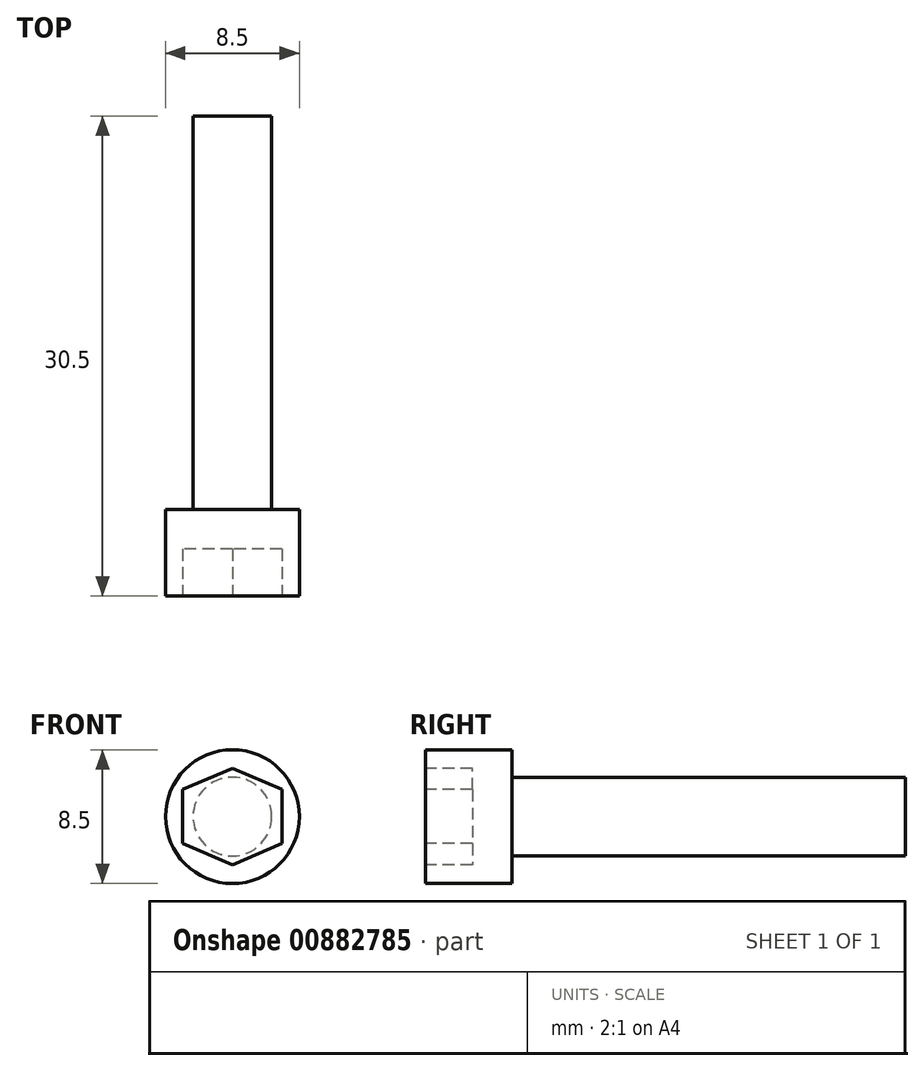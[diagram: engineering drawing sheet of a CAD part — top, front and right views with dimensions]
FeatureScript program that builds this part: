
annotation { "Feature Type Name" : "Feature", "Feature Type Description" : "" }
export const myFeature = defineFeature(function(context is Context, id is Id, definition is map)
    precondition{}
    {
        {
            var Q0;
            Q0=qCreatedBy(makeId("Front.planeOp"),FACE);
            var sketch = newSketch(context, id + "F0", { "sketchPlane" : qUnion([Q0])});
            skCircle(sketch, "E0", {"center": v(0, 0) * mm, "radius": 4.25 * mm});
            skSolve(sketch);
        }
        {
            var Q0;
            Q0 = qSketchRegion(id + "F0", true);
            extrude(context, id + "F1", {"entities" : qUnion([Q0]), "depth" : 5.5 * mm, "offsetDistance" : 25.4 * mm});
        }
        {
            var Q0;
            Q0=makeQuery(id+"F1.opExtrude","CAP_FACE",FACE,{"disambiguationData":[OSD([sQuery(id+"F0.wireOp",EDGE,"E0")])],"isStart":false});
            var sketch = newSketch(context, id + "F2", { "sketchPlane" : qUnion([Q0])});
            skLineSegment(sketch, "E1", {"start": v(0, 4.25) * mm, "end": v(0, -4.25) * mm});
            skLineSegment(sketch, "E2", {"start": v(4.25, 0) * mm, "end": v(-4.25, 0) * mm});
            skLineSegment(sketch, "E3", {"start": v(0, 3.07) * mm, "end": v(-3.15, 1.71) * mm});
            skLineSegment(sketch, "E4", {"start": v(-3.15, 1.71) * mm, "end": v(-3.15, -1.71) * mm});
            skLineSegment(sketch, "E5", {"start": v(-3.15, -1.71) * mm, "end": v(0, -3.07) * mm});
            skLineSegment(sketch, "E6", {"start": v(0, -3.07) * mm, "end": v(3.15, -1.71) * mm});
            skLineSegment(sketch, "E7", {"start": v(3.15, -1.71) * mm, "end": v(3.15, 1.71) * mm});
            skLineSegment(sketch, "E8", {"start": v(3.15, 1.71) * mm, "end": v(0, 3.07) * mm});
            skSolve(sketch);
        }
        {
            var Q0;
            Q0 = qSketchRegion(id + "F2", true);
            extrude(context, id + "F3", {"entities" : qUnion([Q0]), "operationType" : NewBodyOperationType.REMOVE, "oppositeDirection" : true, "depth" : 3 * mm, "offsetDistance" : 25.4 * mm});
        }
        {
            var Q0;
            Q0=makeQuery(id+"F1.opExtrude","CAP_FACE",FACE,{"disambiguationData":[OSD([sQuery(id+"F0.wireOp",EDGE,"E0")])],"isStart":true});
            var sketch = newSketch(context, id + "F4", { "sketchPlane" : qUnion([Q0])});
            skCircle(sketch, "E9", {"center": v(0, 0) * mm, "radius": 2.5 * mm});
            skSolve(sketch);
        }
        {
            var Q0;
            Q0 = qSketchRegion(id + "F4", true);
            extrude(context, id + "F5", {"entities" : qUnion([Q0]), "operationType" : NewBodyOperationType.ADD, "depth" : 25 * mm, "offsetDistance" : 25.4 * mm});
        }
    });
